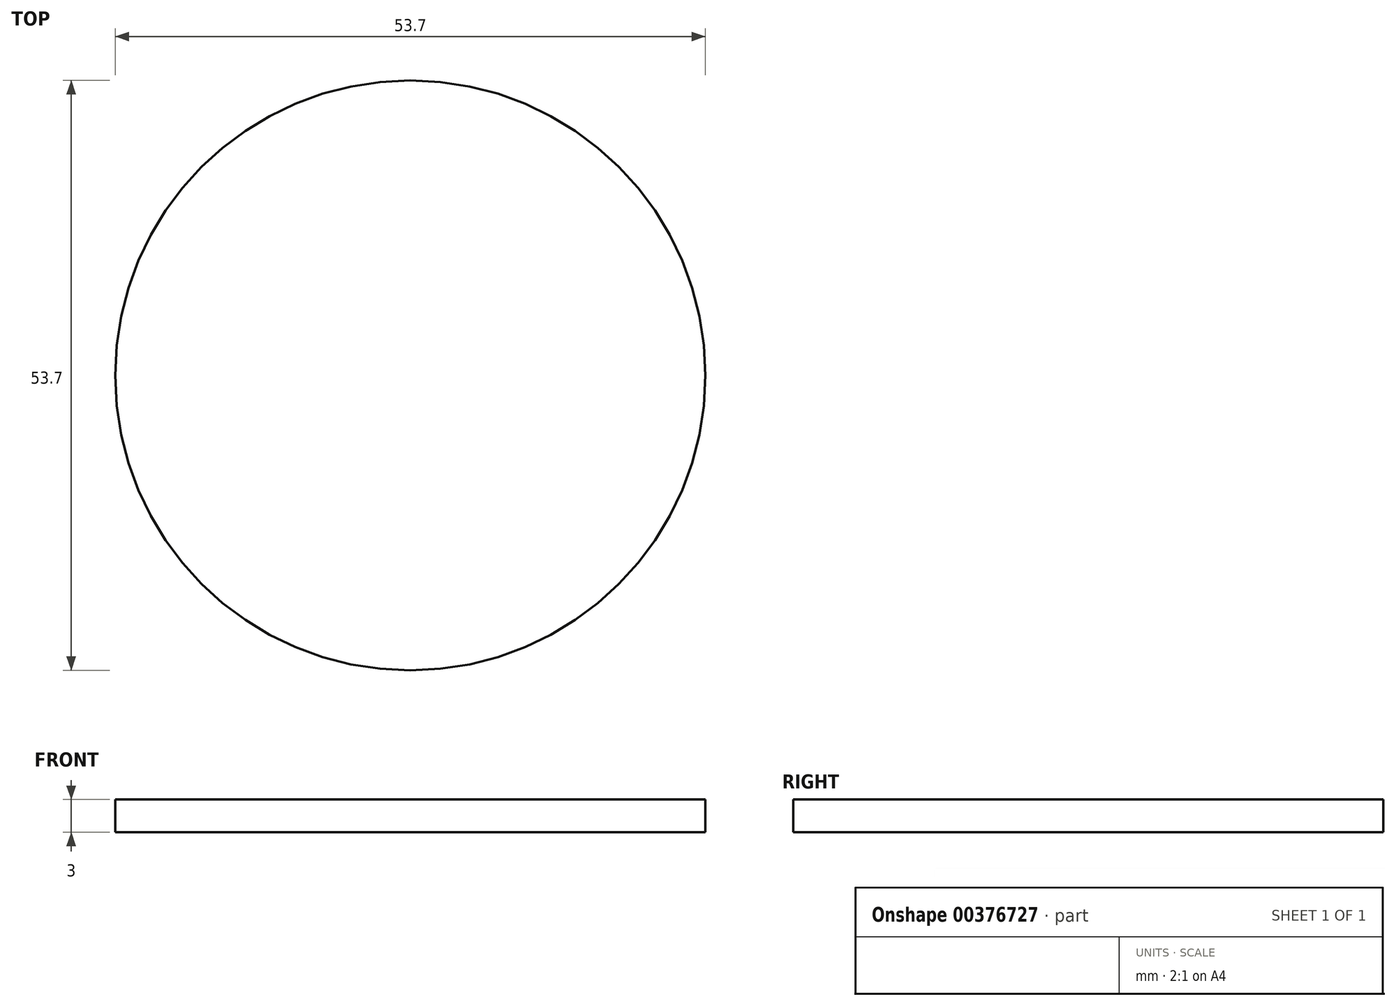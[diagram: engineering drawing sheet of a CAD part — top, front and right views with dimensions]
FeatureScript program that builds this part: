
annotation { "Feature Type Name" : "Feature", "Feature Type Description" : "" }
export const myFeature = defineFeature(function(context is Context, id is Id, definition is map)
    precondition{}
    {
        {
            var Q0;
            Q0=qCreatedBy(makeId("Top.planeOp"),FACE);
            var sketch = newSketch(context, id + "F0", { "sketchPlane" : qUnion([Q0])});
            skCircle(sketch, "E0", {"center": v(0, 0) * mm, "radius": 26.85 * mm});
            skSolve(sketch);
        }
        {
            var Q0;
            Q0=makeQuery(id+"F0.imprint","IMPRINT",FACE,{"disambiguationData":[TD([[makeQuery(id+"F0.imprint","IMPRINT",EDGE,{"derivedFrom":sQuery(id+"F0.wireOp",EDGE,"E0")}),1.0]])]});
            extrude(context, id + "F1", {"entities" : qUnion([Q0]), "depth" : 3 * mm});
        }
    });
